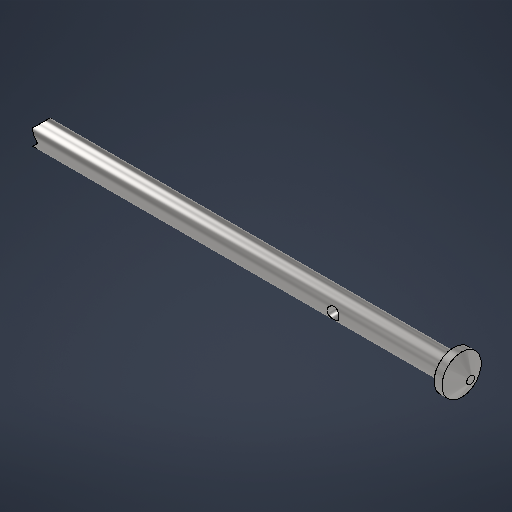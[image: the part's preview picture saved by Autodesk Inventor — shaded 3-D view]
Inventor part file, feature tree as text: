
AUTODESK INVENTOR PART (.ipt)
format: ipt  version: 2025.3 (Build 293356000, 356)  size: 239,104 bytes
history: native  units: mm
features: sketch x1, revolve x1, extrude x1
ambient origin geometry x8: Origin, YZ Plane, XZ Plane, XY Plane, X Axis, Y Axis, Z Axis, Center Point
bodies: Solid1 (feature_tree)
feature tree (3):
  sketch  "Sketch1"  dims[d0=6.0mm d2=60.0deg d3=2.0mm d4=10.0mm d5=2.0mm d6=110.0mm d7=360.0deg d8=0.0mm d9=0.0mm d10=3.0mm d14=2.0mm d16=32.0mm d13=0.872665mm]
  revolve  "Revolution1"  Angle=60.0deg
  extrude  "Extrusion1"  Depth=3.0mm
